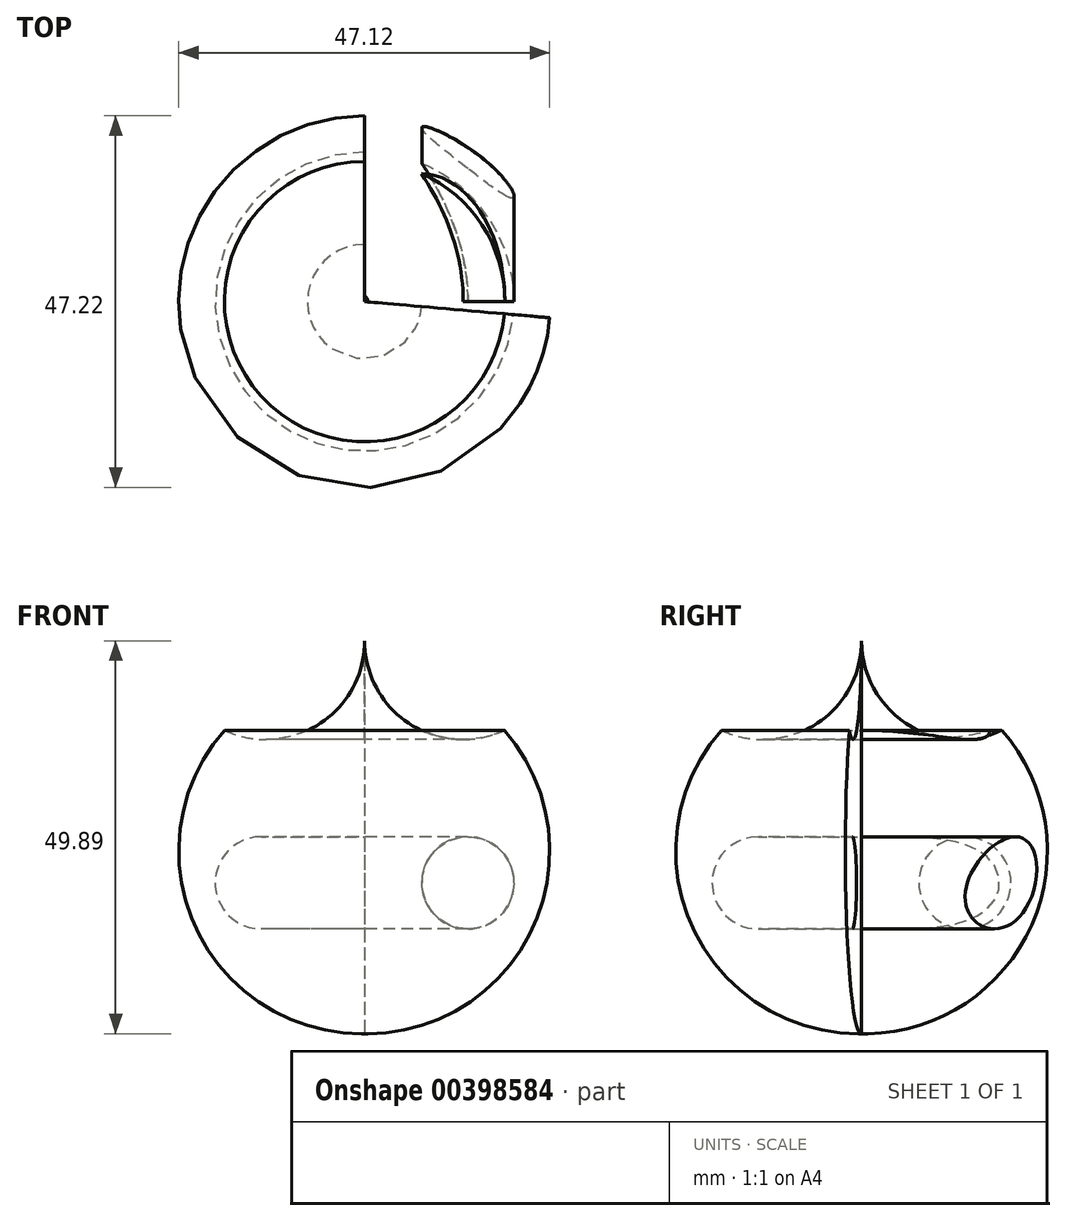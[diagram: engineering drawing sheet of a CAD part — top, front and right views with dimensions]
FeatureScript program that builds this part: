
annotation { "Feature Type Name" : "Feature", "Feature Type Description" : "" }
export const myFeature = defineFeature(function(context is Context, id is Id, definition is map)
    precondition{}
    {
        {
            var Q0;
            Q0=qCreatedBy(makeId("Front.planeOp"),FACE);
            var sketch = newSketch(context, id + "F0", { "sketchPlane" : qUnion([Q0])});
            skLineSegment(sketch, "E0", {"start": v(-60.01, 67.1) * mm, "end": v(-60.01, 17.2) * mm});
            skArc(sketch, "E1", {"start": v(-60.01, 67.1) * mm, "mid": v(-54.22, 56.53) * mm, "end": v(-42.2, 55.74) * mm});
            skArc(sketch, "E2", {"start": v(-60.01, 17.2) * mm, "mid": v(-38.55, 30.67) * mm, "end": v(-42.2, 55.74) * mm});
            skCircle(sketch, "E3", {"center": v(-46.89, 36.36) * mm, "radius": 5.86 * mm});
            skSolve(sketch);
        }
        {
            var Q0;
            Q0 = qSketchRegion(id + "F0", true);
            var Q1;
            Q1=sQuery(id+"F0.wireOp",EDGE,"E0");
            revolve(context, id + "F1", {"entities" : qUnion([Q0]), "axis" : qUnion([Q1]), "revolveType" : RevolveType.ONE_DIRECTION, "oppositeDirection" : true, "angle" : 355 * degree});
        }
        {
            var Q0;
            Q0 = qSketchRegion(id + "F0", true);
            extrude(context, id + "F2", {"entities" : qUnion([Q0]), "operationType" : NewBodyOperationType.REMOVE, "endBound" : BoundingType.THROUGH_ALL, "oppositeDirection" : true, "depth" : 25.4 * mm});
        }
    });
